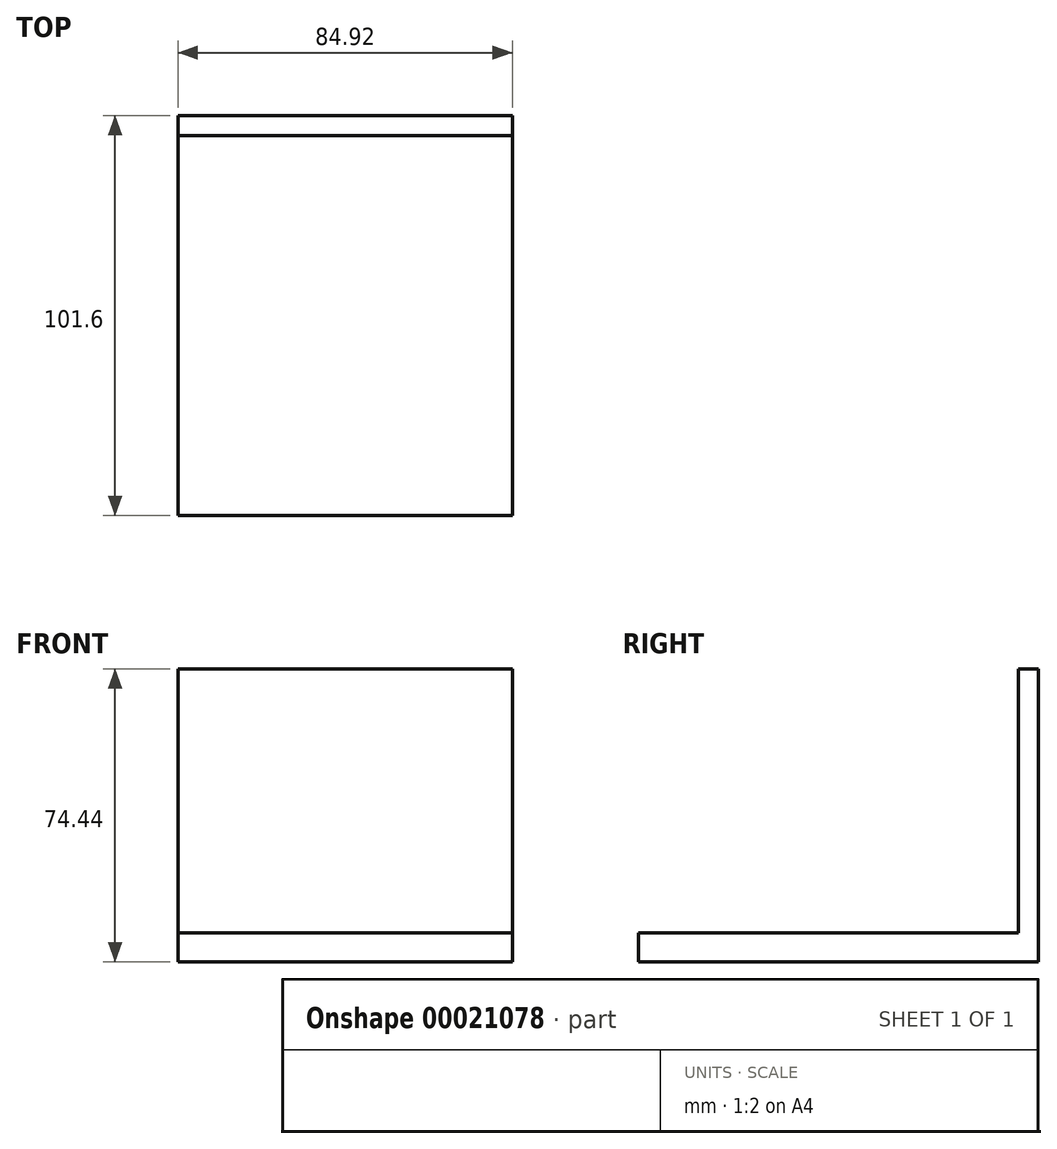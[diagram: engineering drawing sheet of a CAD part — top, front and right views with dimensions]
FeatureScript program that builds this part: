
annotation { "Feature Type Name" : "Feature", "Feature Type Description" : "" }
export const myFeature = defineFeature(function(context is Context, id is Id, definition is map)
    precondition{}
    {
        {
            var Q0;
            Q0=qCreatedBy(makeId("Front.planeOp"),FACE);
            var sketch = newSketch(context, id + "F0", { "sketchPlane" : qUnion([Q0])});
            skLineSegment(sketch, "E0.rect.bottom", {"start": v(-42.46, 0) * mm, "end": v(42.46, 0) * mm});
            skLineSegment(sketch, "E0.rect.top", {"start": v(-42.46, 67.05) * mm, "end": v(42.46, 67.05) * mm});
            skLineSegment(sketch, "E0.rect.left", {"start": v(-42.46, 0) * mm, "end": v(-42.46, 67.05) * mm});
            skLineSegment(sketch, "E0.rect.right", {"start": v(42.46, 0) * mm, "end": v(42.46, 67.05) * mm});
            skPoint(sketch, "E0.rect.middle", {"position": v(0, 33.52) * mm});
            skLineSegment(sketch, "E1.rect.top", {"start": v(-42.46, -7.4) * mm, "end": v(42.46, -7.4) * mm});
            skLineSegment(sketch, "E1.rect.left", {"start": v(-42.46, 0) * mm, "end": v(-42.46, -7.4) * mm});
            skLineSegment(sketch, "E1.rect.right", {"start": v(42.46, 0) * mm, "end": v(42.46, -7.4) * mm});
            skPoint(sketch, "E1.rect.middle", {"position": v(0, -3.7) * mm});
            skSolve(sketch);
        }
        {
            var Q0;
            Q0=makeQuery(id+"F0.imprint","IMPRINT",FACE,{"disambiguationData":[TD([[makeQuery(id+"F0.imprint","IMPRINT",EDGE,{"derivedFrom":sQuery(id+"F0.wireOp",EDGE,"E1.rect.top")}),1.0]])]});
            extrude(context, id + "F1", {"entities" : qUnion([Q0]), "depth" : 101.6 * mm});
        }
        {
            var Q0;
            Q0=makeQuery(id+"F0.imprint","IMPRINT",FACE,{"disambiguationData":[TD([[makeQuery(id+"F0.imprint","IMPRINT",EDGE,{"derivedFrom":sQuery(id+"F0.wireOp",EDGE,"E0.rect.top")}),-1.0]])]});
            extrude(context, id + "F2", {"entities" : qUnion([Q0]), "operationType" : NewBodyOperationType.ADD, "depth" : 5.08 * mm});
        }
    });
